FCSTD DOCUMENT  (FreeCAD 1.2R20251230 (Git shallow))
Label: smart_glasses_0
License: Creative Commons Attribution 4.0
LicenseURL: https://creativecommons.org/licenses/by/4.0/
objects: Sketcher::SketchObject×2, App::Point×1, PartDesign::Body×1
note: 5 computed .brp shape members not serialized (recipe doc carries the construction recipe); baked Part::Feature solids carry a one-line shape summary decoded from their .brp

FEATURE [App::Point] Origin001  label="原点"
  Role = Origin
FEATURE [Sketcher::SketchObject] Sketch
  ArcFitTolerance = 1e-06
  AttachmentSupport = -> [Origin]
  ExternalTypes = [0]
  FullyConstrained = false
  MakeInternals = false
  MapMode = 5
  sketch-geometry (83):
    g0: LineSegment StartX=-44.6431 StartY=-12.8691 StartZ=0 EndX=-49.4299 EndY=18.6606 EndZ=0
    g1: LineSegment StartX=-39.4718 StartY=40.2018 StartZ=0 EndX=-48.5995 EndY=23.3988 EndZ=0
    g2: LineSegment StartX=-37.4949 StartY=42.2431 StartZ=0 EndX=-35.6096 EndY=43.347 EndZ=0
    g3: LineSegment StartX=-34.9116 StartY=42.6805 StartZ=0 EndX=-45.8946 EndY=21.7585 EndZ=0
    g4: LineSegment StartX=-46.1795 StartY=20.2606 StartZ=0 EndX=-42.6348 EndY=-12.6091 EndZ=0
    g5: LineSegment StartX=-43.5009 StartY=-13.7035 StartZ=0 EndX=-43.5351 EndY=-13.7077 EndZ=0
    g6: ArcOfCircle CenterX=-41.9638 CenterY=19.7941 CenterZ=0 NormalX=0 NormalY=0 NormalZ=1 AngleXU=0 Radius=7.5516 StartAngle=2.64397 EndAngle=3.29226
    g7: GeomPoint [constr] X=-49.8107 Y=21.1692 Z=0
    g8: ArcOfCircle CenterX=-34.8202 CenterY=37.6749 CenterZ=0 NormalX=0 NormalY=0 NormalZ=1 AngleXU=0 Radius=5.29359 StartAngle=2.10048 EndAngle=2.64397
    g9: GeomPoint [constr] X=-38.7677 Y=41.4979 Z=0
    g10: ArcOfCircle CenterX=-35.356 CenterY=42.9138 CenterZ=0 NormalX=0 NormalY=0 NormalZ=1 AngleXU=0 Radius=0.501906 StartAngle=5.79978 EndAngle=8.38366
    g11: GeomPoint [constr] X=-34.0968 Y=44.2327 Z=0
    g12: ArcOfCircle CenterX=-43.576 CenterY=20.5414 CenterZ=0 NormalX=0 NormalY=0 NormalZ=1 AngleXU=0 Radius=2.61862 StartAngle=2.65819 EndAngle=3.24902
    g13: GeomPoint [constr] X=-46.265 Y=21.0529 Z=0
    g14: ArcOfCircle CenterX=-43.6244 CenterY=-12.7158 CenterZ=0 NormalX=0 NormalY=0 NormalZ=1 AngleXU=0 Radius=0.995334 StartAngle=4.83674 EndAngle=6.39061
    g15: GeomPoint [constr] X=-42.5298 Y=-13.5821 Z=0
    g16: ArcOfCircle CenterX=-43.6586 CenterY=-12.7196 CenterZ=0 NormalX=0 NormalY=0 NormalZ=1 AngleXU=0 Radius=0.995804 StartAngle=3.29226 EndAngle=4.83674
    g17: ArcOfCircle CenterX=35.3756 CenterY=33.9263 CenterZ=0 NormalX=0 NormalY=0 NormalZ=1 AngleXU=0 Radius=14.9602 StartAngle=0.189378 EndAngle=3.00877
    g18: ArcOfCircle CenterX=26.7496 CenterY=16.2061 CenterZ=0 NormalX=0 NormalY=0 NormalZ=1 AngleXU=0 Radius=7.90499 StartAngle=3.03877 EndAngle=5.2827
    g19: LineSegment StartX=-113.726 StartY=52.4777 StartZ=0 EndX=-93.6115 EndY=39.4134 EndZ=0
    g20: LineSegment StartX=-93.6115 StartY=39.4134 StartZ=0 EndX=-113.312 EndY=28.5265 EndZ=0
    g21: LineSegment StartX=-108.049 StartY=31.0762 StartZ=0 EndX=-78.0588 EndY=26.8676 EndZ=0
    g22: ArcOfEllipse CenterX=-126.741 CenterY=52.1553 CenterZ=0 NormalX=0 NormalY=0 NormalZ=1 MajorRadius=2.45999 MinorRadius=2.01302 AngleXU=-0.349856 StartAngle=5.95659 EndAngle=6.68646
    g23: LineSegment [constr] StartX=-124.43 StartY=51.3121 StartZ=0 EndX=-129.052 EndY=52.9985 EndZ=0
    g24: LineSegment [constr] StartX=-126.051 StartY=54.0464 StartZ=0 EndX=-127.431 EndY=50.2642 EndZ=0
    g25: GeomPoint [constr] X=-125.413 Y=51.6706 Z=0
    g26: GeomPoint [constr] X=-128.069 Y=52.64 Z=0
    g27: ArcOfEllipse CenterX=-115.561 CenterY=46.8151 CenterZ=0 NormalX=0 NormalY=0 NormalZ=1 MajorRadius=2.45932 MinorRadius=1.51775 AngleXU=-2.21018 StartAngle=2.49555 EndAngle=7.74185
    g28: LineSegment [constr] StartX=-117.028 StartY=44.8416 StartZ=0 EndX=-114.093 EndY=48.7886 EndZ=0
    g29: LineSegment [constr] StartX=-114.343 StartY=45.9094 StartZ=0 EndX=-116.779 EndY=47.7207 EndZ=0
    g30: GeomPoint [constr] X=-116.716 Y=45.2622 Z=0
    g31: GeomPoint [constr] X=-114.406 Y=48.368 Z=0
    g32: ArcOfCircle CenterX=-99.3737 CenterY=57.4862 CenterZ=0 NormalX=0 NormalY=0 NormalZ=1 AngleXU=0 Radius=3.25236 StartAngle=3.75206 EndAngle=5.09277
    g33: ArcOfParabola CenterX=-131.419 CenterY=69.631 CenterZ=0 NormalX=0 NormalY=0 NormalZ=1 Focal=4.59446 AngleXU=2.52724 StartAngle=-2.27497 EndAngle=-0.0447105
    g34: GeomPoint [constr] X=-135.174 Y=72.2794 Z=0
    g35: LineSegment [constr] StartX=-131.419 StartY=69.631 StartZ=0 EndX=-135.174 EndY=72.2794 EndZ=0
    g36: ArcOfParabola CenterX=-128.34 CenterY=69.7487 CenterZ=0 NormalX=0 NormalY=0 NormalZ=1 Focal=4.97602 AngleXU=2.86921 StartAngle=1.54307 EndAngle=1.92024
    g37: GeomPoint [constr] X=-133.133 Y=71.0874 Z=0
    g38: LineSegment [constr] StartX=-128.34 StartY=69.7487 StartZ=0 EndX=-133.133 EndY=71.0874 EndZ=0
    g39: Ellipse CenterX=-117.407 CenterY=70.4858 CenterZ=0 NormalX=0 NormalY=0 NormalZ=1 MajorRadius=4.9111 MinorRadius=1.89223 AngleXU=3.12808
    g40: LineSegment [constr] StartX=-122.318 StartY=70.5521 StartZ=0 EndX=-112.497 EndY=70.4194 EndZ=0
    g41: LineSegment [constr] StartX=-117.433 StartY=68.5937 StartZ=0 EndX=-117.382 EndY=72.3778 EndZ=0
    g42: GeomPoint [constr] X=-121.939 Y=70.547 Z=0
    g43: GeomPoint [constr] X=-112.876 Y=70.4245 Z=0
    g44: Ellipse CenterX=-118.404 CenterY=64.6562 CenterZ=0 NormalX=0 NormalY=0 NormalZ=1 MajorRadius=4.82559 MinorRadius=3.73689 AngleXU=2.91718
    g45: LineSegment [constr] StartX=-123.109 StartY=65.7301 StartZ=0 EndX=-113.7 EndY=63.5823 EndZ=0
    g46: LineSegment [constr] StartX=-119.236 StartY=61.013 StartZ=0 EndX=-117.573 EndY=68.2994 EndZ=0
    g47: GeomPoint [constr] X=-121.381 Y=65.3356 Z=0
    g48: GeomPoint [constr] X=-115.428 Y=63.9767 Z=0
    g49: LineSegment StartX=-140.751 StartY=67.5074 StartZ=0 EndX=-140.751 EndY=62.2907 EndZ=0
    g50: LineSegment StartX=-140.202 StartY=61.7414 StartZ=0 EndX=-138.693 EndY=61.7414 EndZ=0
    g51: LineSegment StartX=-138.143 StartY=62.2907 StartZ=0 EndX=-138.143 EndY=67.5074 EndZ=0
    g52: LineSegment StartX=-138.693 StartY=68.0568 StartZ=0 EndX=-140.202 EndY=68.0568 EndZ=0
    g53: ArcOfCircle CenterX=-140.202 CenterY=67.5074 CenterZ=0 NormalX=0 NormalY=0 NormalZ=1 AngleXU=0 Radius=0.549355 StartAngle=1.5708 EndAngle=3.14159
    g54: ArcOfCircle CenterX=-140.202 CenterY=62.2907 CenterZ=0 NormalX=0 NormalY=0 NormalZ=1 AngleXU=0 Radius=0.549355 StartAngle=3.14159 EndAngle=4.71239
    g55: ArcOfCircle CenterX=-138.693 CenterY=62.2907 CenterZ=0 NormalX=0 NormalY=0 NormalZ=1 AngleXU=0 Radius=0.549355 StartAngle=4.71239 EndAngle=6.28319
    g56: ArcOfCircle CenterX=-138.693 CenterY=67.5074 CenterZ=0 NormalX=0 NormalY=0 NormalZ=1 AngleXU=0 Radius=0.549355 StartAngle=0 EndAngle=1.5708
    g57: GeomPoint [constr] X=-140.751 Y=68.0568 Z=0
    g58: GeomPoint [constr] X=-138.143 Y=61.7414 Z=0
    g59: ArcOfCircle CenterX=-131.649 CenterY=63.6079 CenterZ=0 NormalX=0 NormalY=0 NormalZ=1 AngleXU=0 Radius=3.47763 StartAngle=2.83572 EndAngle=4.28444
    g60: ArcOfCircle CenterX=-132.978 CenterY=60.6931 CenterZ=0 NormalX=0 NormalY=0 NormalZ=1 AngleXU=0 Radius=0.273918 StartAngle=4.28444 EndAngle=7.42603
    g61: ArcOfCircle CenterX=-134.704 CenterY=64.5726 CenterZ=0 NormalX=0 NormalY=0 NormalZ=1 AngleXU=0 Radius=0.273918 StartAngle=5.97732 EndAngle=9.11891
    g62: ArcOfCircle CenterX=-131.649 CenterY=63.6079 CenterZ=0 NormalX=0 NormalY=0 NormalZ=1 AngleXU=0 Radius=2.92979 StartAngle=2.83572 EndAngle=4.28444
    g63-g71: Circle [constr] x9 (B-spline internal-alignment scaffolding for g72; pole/knot coordinates omitted)
    g72: BSplineCurve PolesCount=9 KnotsCount=10 Degree=3 IsPeriodic=1
    g73-g82: GeomPoint [constr] x10 (B-spline internal-alignment scaffolding for g72; pole/knot coordinates omitted)
  constraints (59):
    c: PointOnObject(g7,g1)
    c: PointOnObject(g7,g0)
    c: Tangent(g1,g6) = -1.5708
    c: Tangent(g0,g6) = 1.5708
    c: PointOnObject(g9,g1)
    c: Tangent(g1,g8) = -1.5708
    c: PointOnObject(g11,g2)
    c: PointOnObject(g11,g3)
    c: Tangent(g2,g10) = 1.5708
    c: Tangent(g3,g10) = 1.5708
    c: PointOnObject(g13,g3)
    c: PointOnObject(g13,g4)
    c: Tangent(g3,g12) = -1.5708
    c: Tangent(g4,g12) = -1.5708
    c: PointOnObject(g15,g4)
    c: PointOnObject(g15,g5)
    c: Tangent(g4,g14) = 1.5708
    c: Tangent(g5,g14) = 1.5708
    c: Tangent(g0,g16) = 1.5708
    c: Tangent(g5,g16) = 1.5708
    c: Coincident(g20,g19)
    c: InternalAlignment(g23-g26 -> g22) x4
    c: InternalAlignment(g28-g31 -> g27) x4
    c: InternalAlignment(g34,g33)
    c: InternalAlignment(g35,g33)
    c: InternalAlignment(g37,g36)
    c: InternalAlignment(g38,g36)
    c: PointOnObject(g36,g35)
    c: InternalAlignment(g40-g43 -> g39) x4
    c: InternalAlignment(g45-g48 -> g44) x4
    c: Tangent(g49,g53) = -1.5708
    c: Tangent(g49,g54) = -1.5708
    c: Tangent(g50,g54) = -1.5708
    c: Tangent(g50,g55) = -1.5708
    c: Tangent(g51,g55) = -1.5708
    c: Tangent(g51,g56) = -1.5708
    c: Tangent(g52,g56) = -1.5708
    c: Tangent(g52,g53) = -1.5708
    c: Vertical(g49)
    c: Vertical(g51)
    c: Horizontal(g50)
    c: Horizontal(g52)
    c: Equal(g53,g54)
    c: Equal(g54,g55)
    c: Equal(g55,g56)
    c: PointOnObject(g57,g49)
    c: PointOnObject(g57,g52)
    c: PointOnObject(g58,g50)
    c: PointOnObject(g58,g51)
    c: Coincident(g59,g62)
    c: Tangent(g62,g61) = 1.5708
    c: Tangent(g62,g60) = 1.5708
    c: Tangent(g59,g61) = -1.5708
    c: Tangent(g59,g60) = -1.5708
    c: Weight(g63) = 1
    c: Equal(g63, g64-g71) x8
    c: InternalAlignment(g63-g71 -> g72) x9
    c: InternalAlignment(g73-g82 -> g72) x10
    c: PointOnObject(g65,g63)
FEATURE [Sketcher::SketchObject] Sketch001
  ArcFitTolerance = 1e-06
  AttachmentSupport = -> [Origin]
  ExternalTypes = [0]
  FullyConstrained = false
  MakeInternals = false
  MapMode = 5
  sketch-geometry (132):
    g0: LineSegment StartX=-179.096 StartY=100.414 StartZ=0 EndX=-133.628 EndY=107.258 EndZ=0
    g1: LineSegment StartX=-133.628 StartY=107.258 StartZ=0 EndX=-131.954 EndY=85.1217 EndZ=0
    g2: LineSegment StartX=-131.954 StartY=85.1217 StartZ=0 EndX=-85.4499 EndY=81.0294 EndZ=0
    g3: LineSegment StartX=-85.4499 StartY=81.0294 StartZ=0 EndX=-101.633 EndY=62.2129 EndZ=0
    g4: LineSegment StartX=-101.633 StartY=62.2129 StartZ=0 EndX=-169.157 EndY=62.2129 EndZ=0
    g5: LineSegment StartX=-169.157 StartY=62.2129 StartZ=0 EndX=-179.096 EndY=100.414 EndZ=0
    g6: LineSegment StartX=-171.369 StartY=43.8261 StartZ=0 EndX=-101.654 EndY=43.8261 EndZ=0
    g7: ArcOfCircle CenterX=80.0712 CenterY=191.162 CenterZ=0 NormalX=0 NormalY=0 NormalZ=1 AngleXU=0 Radius=10 StartAngle=5.44193 EndAngle=7.53633
    g8: ArcOfCircle CenterX=137.521 CenterY=114.594 CenterZ=0 NormalX=0 NormalY=0 NormalZ=1 AngleXU=0 Radius=8.45744 StartAngle=3.76206 EndAngle=7.56382
    g9: ArcOfEllipse CenterX=195.187 CenterY=133.858 CenterZ=0 NormalX=0 NormalY=0 NormalZ=1 MajorRadius=31.4877 MinorRadius=12.413 AngleXU=-1.90676 StartAngle=1.03899 EndAngle=4.30453
    g10: LineSegment [constr] StartX=184.806 StartY=104.131 StartZ=0 EndX=205.568 EndY=163.586 EndZ=0
    g11: LineSegment [constr] StartX=206.906 StartY=129.766 StartZ=0 EndX=183.468 EndY=137.951 EndZ=0
    g12: GeomPoint [constr] X=185.647 Y=106.539 Z=0
    g13: GeomPoint [constr] X=204.728 Y=161.178 Z=0
    g14: Circle CenterX=54.931 CenterY=95.725 CenterZ=0 NormalX=0 NormalY=0 NormalZ=1 AngleXU=0 Radius=12.9332
    g15: Circle CenterX=95.9598 CenterY=131.115 CenterZ=0 NormalX=0 NormalY=0 NormalZ=1 AngleXU=0 Radius=21.3432
    g16: Ellipse CenterX=165.425 CenterY=181.665 CenterZ=0 NormalX=0 NormalY=0 NormalZ=1 MajorRadius=13.6492 MinorRadius=11.0941 AngleXU=-2.53499
    g17: LineSegment [constr] StartX=154.211 StartY=173.883 StartZ=0 EndX=176.639 EndY=189.446 EndZ=0
    g18: LineSegment [constr] StartX=171.749 StartY=172.55 StartZ=0 EndX=159.1 EndY=190.779 EndZ=0
    g19: GeomPoint [constr] X=158.892 Y=177.132 Z=0
    g20: GeomPoint [constr] X=171.957 Y=186.197 Z=0
    g21: Ellipse CenterX=127.198 CenterY=157.762 CenterZ=0 NormalX=0 NormalY=0 NormalZ=1 MajorRadius=15.291 MinorRadius=8.35315 AngleXU=0.65909
    g22: LineSegment [constr] StartX=139.287 StartY=167.126 StartZ=0 EndX=115.11 EndY=148.397 EndZ=0
    g23: LineSegment [constr] StartX=122.083 StartY=164.365 StartZ=0 EndX=132.314 EndY=151.158 EndZ=0
    g24: GeomPoint [constr] X=137.324 Y=165.605 Z=0
    g25: GeomPoint [constr] X=117.073 Y=149.918 Z=0
    g26: LineSegment StartX=47.3976 StartY=-33.3055 StartZ=0 EndX=47.3976 EndY=-42.2341 EndZ=0
    g27: LineSegment StartX=51.8487 StartY=-46.6851 StartZ=0 EndX=57.1613 EndY=-46.6851 EndZ=0
    g28: LineSegment StartX=61.6123 StartY=-42.2341 StartZ=0 EndX=61.6123 EndY=-33.3055 EndZ=0
    g29: LineSegment StartX=57.1613 StartY=-28.8544 StartZ=0 EndX=51.8487 EndY=-28.8544 EndZ=0
    g30: ArcOfCircle CenterX=51.8487 CenterY=-33.3055 CenterZ=0 NormalX=0 NormalY=0 NormalZ=1 AngleXU=0 Radius=4.45108 StartAngle=1.5708 EndAngle=3.14159
    g31: ArcOfCircle CenterX=51.8487 CenterY=-42.2341 CenterZ=0 NormalX=0 NormalY=0 NormalZ=1 AngleXU=0 Radius=4.45108 StartAngle=3.14159 EndAngle=4.71239
    g32: ArcOfCircle CenterX=57.1613 CenterY=-42.2341 CenterZ=0 NormalX=0 NormalY=0 NormalZ=1 AngleXU=0 Radius=4.45108 StartAngle=4.71239 EndAngle=6.28319
    g33: ArcOfCircle CenterX=57.1613 CenterY=-33.3055 CenterZ=0 NormalX=0 NormalY=0 NormalZ=1 AngleXU=0 Radius=4.45108 StartAngle=0 EndAngle=1.5708
    g34: GeomPoint [constr] X=47.3976 Y=-28.8544 Z=0
    g35: GeomPoint [constr] X=61.6123 Y=-46.6851 Z=0
    g36: LineSegment StartX=120.217 StartY=-40.0765 StartZ=0 EndX=120.217 EndY=-61.8974 EndZ=0
    g37: LineSegment StartX=120.217 StartY=-61.8974 StartZ=0 EndX=151.39 EndY=-61.8974 EndZ=0
    g38: LineSegment StartX=151.39 StartY=-61.8974 StartZ=0 EndX=151.39 EndY=-40.0765 EndZ=0
    g39: LineSegment StartX=151.39 StartY=-40.0765 StartZ=0 EndX=120.217 EndY=-40.0765 EndZ=0
    g40: LineSegment StartX=56.126 StartY=-66.885 StartZ=0 EndX=56.126 EndY=-84.0923 EndZ=0
    g41: LineSegment StartX=56.126 StartY=-84.0923 StartZ=0 EndX=93.7825 EndY=-84.0923 EndZ=0
    g42: LineSegment StartX=93.7825 StartY=-84.0923 StartZ=0 EndX=93.7825 EndY=-66.885 EndZ=0
    g43: LineSegment StartX=93.7825 StartY=-66.885 StartZ=0 EndX=56.126 EndY=-66.885 EndZ=0
    g44: GeomPoint [constr] X=74.9542 Y=-75.4887 Z=0
    g45: LineSegment StartX=-629.082 StartY=-206.086 StartZ=0 EndX=-663.995 EndY=-61.1739 EndZ=0
    g46: LineSegment StartX=-663.995 StartY=-61.1739 StartZ=0 EndX=-772.036 EndY=-163.866 EndZ=0
    g47: LineSegment StartX=-772.036 StartY=-163.866 StartZ=0 EndX=-629.082 EndY=-206.086 EndZ=0
    g48: Circle [constr] CenterX=-688.371 CenterY=-143.709 CenterZ=0 NormalX=0 NormalY=0 NormalZ=1 AngleXU=0 Radius=86.0589
    g49: LineSegment StartX=-350.546 StartY=-239.436 StartZ=0 EndX=-378.338 EndY=-68.3619 EndZ=0
    g50: LineSegment StartX=-378.338 StartY=-68.3619 StartZ=0 EndX=-549.412 EndY=-96.1537 EndZ=0
    g51: LineSegment StartX=-549.412 StartY=-96.1537 StartZ=0 EndX=-521.62 EndY=-267.228 EndZ=0
    g52: LineSegment StartX=-521.62 StartY=-267.228 StartZ=0 EndX=-350.546 EndY=-239.436 EndZ=0
    g53: Circle [constr] CenterX=-449.979 CenterY=-167.795 CenterZ=0 NormalX=0 NormalY=0 NormalZ=1 AngleXU=0 Radius=122.554
    g54: LineSegment StartX=-661.197 StartY=-493.268 StartZ=0 EndX=-642.21 EndY=-409.175 EndZ=0
    g55: LineSegment StartX=-642.21 StartY=-409.175 StartZ=0 EndX=-696.119 EndY=-341.9 EndZ=0
    g56: LineSegment StartX=-696.119 StartY=-341.9 StartZ=0 EndX=-782.328 EndY=-342.101 EndZ=0
    g57: LineSegment StartX=-782.328 StartY=-342.101 StartZ=0 EndX=-835.921 EndY=-409.628 EndZ=0
    g58: LineSegment StartX=-835.921 StartY=-409.628 StartZ=0 EndX=-816.541 EndY=-493.632 EndZ=0
    g59: LineSegment StartX=-816.541 StartY=-493.632 StartZ=0 EndX=-738.781 EndY=-530.855 EndZ=0
    g60: LineSegment StartX=-738.781 StartY=-530.855 StartZ=0 EndX=-661.197 EndY=-493.268 EndZ=0
    g61: Circle [constr] CenterX=-739.014 CenterY=-431.508 CenterZ=0 NormalX=0 NormalY=0 NormalZ=1 AngleXU=0 Radius=99.3466
    g62: LineSegment StartX=-311.02 StartY=-522.913 StartZ=0 EndX=-280.576 EndY=-458.333 EndZ=0
    g63: LineSegment StartX=-280.576 StartY=-458.333 StartZ=0 EndX=-298.766 EndY=-389.293 EndZ=0
    g64: LineSegment StartX=-298.766 StartY=-389.293 StartZ=0 EndX=-357.078 EndY=-348.098 EndZ=0
    g65: LineSegment StartX=-357.078 StartY=-348.098 StartZ=0 EndX=-428.228 EndY=-354.023 EndZ=0
    g66: LineSegment StartX=-428.228 StartY=-354.023 StartZ=0 EndX=-478.923 EndY=-404.296 EndZ=0
    g67: LineSegment StartX=-478.923 StartY=-404.296 StartZ=0 EndX=-485.443 EndY=-475.393 EndZ=0
    g68: LineSegment StartX=-485.443 StartY=-475.393 StartZ=0 EndX=-444.737 EndY=-534.048 EndZ=0
    g69: LineSegment StartX=-444.737 StartY=-534.048 StartZ=0 EndX=-375.852 EndY=-552.815 EndZ=0
    g70: LineSegment StartX=-375.852 StartY=-552.815 StartZ=0 EndX=-311.02 EndY=-522.913 EndZ=0
    g71: Circle [constr] CenterX=-384.514 CenterY=-448.801 CenterZ=0 NormalX=0 NormalY=0 NormalZ=1 AngleXU=0 Radius=104.374
    g72: ArcOfCircle CenterX=-661.197 CenterY=-645.814 CenterZ=0 NormalX=0 NormalY=0 NormalZ=1 AngleXU=0 Radius=43.0061 StartAngle=1.50755 EndAngle=4.64914
    g73: ArcOfCircle CenterX=-475.918 CenterY=-657.549 CenterZ=0 NormalX=0 NormalY=0 NormalZ=1 AngleXU=0 Radius=43.0061 StartAngle=4.64914 EndAngle=7.79073
    g74: LineSegment StartX=-658.479 StartY=-602.894 StartZ=0 EndX=-473.2 EndY=-614.629 EndZ=0
    g75: LineSegment StartX=-663.915 StartY=-688.734 StartZ=0 EndX=-478.636 EndY=-700.469 EndZ=0
    g76: ArcOfCircle CenterX=-2011.29 CenterY=1760.95 CenterZ=0 NormalX=0 NormalY=0 NormalZ=1 AngleXU=0 Radius=100 StartAngle=1.41132 EndAngle=4.55291
    g77: ArcOfCircle CenterX=-1511.29 CenterY=1680.53 CenterZ=0 NormalX=0 NormalY=0 NormalZ=1 AngleXU=0 Radius=100 StartAngle=4.55291 EndAngle=7.6945
    g78: LineSegment StartX=-1995.41 StartY=1859.68 StartZ=0 EndX=-1495.41 EndY=1779.26 EndZ=0
    g79: LineSegment StartX=-2027.17 StartY=1662.22 StartZ=0 EndX=-1527.17 EndY=1581.8 EndZ=0
    g80: ArcOfCircle CenterX=-2249.55 CenterY=1202.8 CenterZ=0 NormalX=0 NormalY=0 NormalZ=1 AngleXU=0 Radius=258.116 StartAngle=4.39919 EndAngle=5.96613
    g81: ArcOfCircle CenterX=-2118.32 CenterY=1159.74 CenterZ=0 NormalX=0 NormalY=0 NormalZ=1 AngleXU=0 Radius=120 StartAngle=5.96613 EndAngle=9.10772
    g82: ArcOfCircle CenterX=-2292.1 CenterY=1071.4 CenterZ=0 NormalX=0 NormalY=0 NormalZ=1 AngleXU=0 Radius=120 StartAngle=1.25759 EndAngle=4.39919
    g83: ArcOfCircle CenterX=-2249.55 CenterY=1202.8 CenterZ=0 NormalX=0 NormalY=0 NormalZ=1 AngleXU=0 Radius=18.1157 StartAngle=4.39919 EndAngle=5.96613
    g84: ArcOfCircle CenterX=-1296.14 CenterY=942.451 CenterZ=0 NormalX=0 NormalY=0 NormalZ=1 AngleXU=0 Radius=264.957 StartAngle=0.28493 EndAngle=2.55295
    g85: ArcOfCircle CenterX=-1118.64 CenterY=994.441 CenterZ=0 NormalX=0 NormalY=0 NormalZ=1 AngleXU=0 Radius=80 StartAngle=3.42652 EndAngle=6.56811
    g86: ArcOfCircle CenterX=-1449.97 CenterY=1045.15 CenterZ=0 NormalX=0 NormalY=0 NormalZ=1 AngleXU=0 Radius=80 StartAngle=2.55295 EndAngle=5.69454
    g87: ArcOfCircle CenterX=-1296.14 CenterY=942.451 CenterZ=0 NormalX=0 NormalY=0 NormalZ=1 AngleXU=0 Radius=104.957 StartAngle=0.28493 EndAngle=2.55295
    g88: LineSegment StartX=-1134.08 StartY=2205.49 StartZ=0 EndX=-500.48 EndY=2205.49 EndZ=0
    g89: LineSegment StartX=-912.628 StartY=2369.53 StartZ=0 EndX=-912.628 EndY=2010.69 EndZ=0
    g90: LineSegment StartX=-1562.63 StartY=1207.41 StartZ=0 EndX=-906.477 EndY=1207.41 EndZ=0
    g91: ArcOfCircle CenterX=413.213 CenterY=2914.61 CenterZ=0 NormalX=0 NormalY=0 NormalZ=1 AngleXU=0 Radius=286.747 StartAngle=6.02951 EndAngle=7.13515
    g92: ArcOfCircle CenterX=634.666 CenterY=2857.2 CenterZ=0 NormalX=0 NormalY=0 NormalZ=1 AngleXU=0 Radius=57.9718 StartAngle=2.88792 EndAngle=6.02951
    g93: ArcOfCircle CenterX=563.862 CenterY=3086.78 CenterZ=0 NormalX=0 NormalY=0 NormalZ=1 AngleXU=0 Radius=57.9718 StartAngle=0.851965 EndAngle=3.99356
    g94: ArcOfCircle CenterX=413.213 CenterY=2914.61 CenterZ=0 NormalX=0 NormalY=0 NormalZ=1 AngleXU=0 Radius=170.803 StartAngle=6.02951 EndAngle=7.13515
    g95: ArcOfCircle CenterX=804.905 CenterY=2914.61 CenterZ=0 NormalX=0 NormalY=0 NormalZ=1 AngleXU=0 Radius=286.747 StartAngle=6.02951 EndAngle=7.13515
    g96: ArcOfCircle CenterX=1026.36 CenterY=2857.2 CenterZ=0 NormalX=0 NormalY=0 NormalZ=1 AngleXU=0 Radius=57.9718 StartAngle=2.88792 EndAngle=6.02951
    g97: ArcOfCircle CenterX=955.554 CenterY=3086.78 CenterZ=0 NormalX=0 NormalY=0 NormalZ=1 AngleXU=0 Radius=57.9718 StartAngle=0.851965 EndAngle=3.99356
    g98: ArcOfCircle CenterX=804.905 CenterY=2914.61 CenterZ=0 NormalX=0 NormalY=0 NormalZ=1 AngleXU=0 Radius=170.803 StartAngle=6.02951 EndAngle=7.13515
    g99: ArcOfCircle CenterX=1196.6 CenterY=2914.61 CenterZ=0 NormalX=0 NormalY=0 NormalZ=1 AngleXU=0 Radius=286.746 StartAngle=6.02951 EndAngle=7.13515
    g100: ArcOfCircle CenterX=1418.05 CenterY=2857.2 CenterZ=0 NormalX=0 NormalY=0 NormalZ=1 AngleXU=0 Radius=57.9717 StartAngle=2.88792 EndAngle=6.02951
    g101: ArcOfCircle CenterX=1347.25 CenterY=3086.78 CenterZ=0 NormalX=0 NormalY=0 NormalZ=1 AngleXU=0 Radius=57.9717 StartAngle=0.851965 EndAngle=3.99356
    g102: ArcOfCircle CenterX=1196.6 CenterY=2914.61 CenterZ=0 NormalX=0 NormalY=0 NormalZ=1 AngleXU=0 Radius=170.803 StartAngle=6.02951 EndAngle=7.13515
    g103: ArcOfCircle CenterX=1588.29 CenterY=2914.61 CenterZ=0 NormalX=0 NormalY=0 NormalZ=1 AngleXU=0 Radius=286.746 StartAngle=6.02951 EndAngle=7.13515
    g104: ArcOfCircle CenterX=1809.74 CenterY=2857.2 CenterZ=0 NormalX=0 NormalY=0 NormalZ=1 AngleXU=0 Radius=57.9717 StartAngle=2.88792 EndAngle=6.02951
    g105: ArcOfCircle CenterX=1738.94 CenterY=3086.78 CenterZ=0 NormalX=0 NormalY=0 NormalZ=1 AngleXU=0 Radius=57.9717 StartAngle=0.851965 EndAngle=3.99356
    g106: ArcOfCircle CenterX=1588.29 CenterY=2914.61 CenterZ=0 NormalX=0 NormalY=0 NormalZ=1 AngleXU=0 Radius=170.803 StartAngle=6.02951 EndAngle=7.13515
    g107: ArcOfCircle CenterX=724.887 CenterY=1883.21 CenterZ=0 NormalX=0 NormalY=0 NormalZ=1 AngleXU=0 Radius=286.747 StartAngle=6.02951 EndAngle=7.13515
    g108: ArcOfCircle CenterX=946.341 CenterY=1825.8 CenterZ=0 NormalX=0 NormalY=0 NormalZ=1 AngleXU=0 Radius=57.9718 StartAngle=2.88792 EndAngle=6.02951
    g109: ArcOfCircle CenterX=875.537 CenterY=2055.39 CenterZ=0 NormalX=0 NormalY=0 NormalZ=1 AngleXU=0 Radius=57.9718 StartAngle=0.851965 EndAngle=3.99356
    g110: ArcOfCircle CenterX=724.887 CenterY=1883.21 CenterZ=0 NormalX=0 NormalY=0 NormalZ=1 AngleXU=0 Radius=170.803 StartAngle=6.02951 EndAngle=7.13515
    g111: ArcOfCircle CenterX=1116.58 CenterY=1883.21 CenterZ=0 NormalX=0 NormalY=0 NormalZ=1 AngleXU=0 Radius=286.746 StartAngle=6.02951 EndAngle=7.13515
    g112: ArcOfCircle CenterX=1338.03 CenterY=1825.8 CenterZ=0 NormalX=0 NormalY=0 NormalZ=1 AngleXU=0 Radius=57.9717 StartAngle=2.88792 EndAngle=6.02951
    g113: ArcOfCircle CenterX=1267.23 CenterY=2055.38 CenterZ=0 NormalX=0 NormalY=0 NormalZ=1 AngleXU=0 Radius=57.9717 StartAngle=0.851965 EndAngle=3.99356
    g114: ArcOfCircle CenterX=1116.58 CenterY=1883.21 CenterZ=0 NormalX=0 NormalY=0 NormalZ=1 AngleXU=0 Radius=170.803 StartAngle=6.02951 EndAngle=7.13515
    g115: ArcOfCircle CenterX=1508.27 CenterY=1883.21 CenterZ=0 NormalX=0 NormalY=0 NormalZ=1 AngleXU=0 Radius=286.747 StartAngle=6.02951 EndAngle=7.13515
    g116: ArcOfCircle CenterX=1729.73 CenterY=1825.8 CenterZ=0 NormalX=0 NormalY=0 NormalZ=1 AngleXU=0 Radius=57.9718 StartAngle=2.88792 EndAngle=6.02951
    g117: ArcOfCircle CenterX=1658.92 CenterY=2055.39 CenterZ=0 NormalX=0 NormalY=0 NormalZ=1 AngleXU=0 Radius=57.9718 StartAngle=0.851965 EndAngle=3.99356
    g118: ArcOfCircle CenterX=1508.27 CenterY=1883.21 CenterZ=0 NormalX=0 NormalY=0 NormalZ=1 AngleXU=0 Radius=170.803 StartAngle=6.02951 EndAngle=7.13515
    g119: ArcOfCircle CenterX=1899.96 CenterY=1883.21 CenterZ=0 NormalX=0 NormalY=0 NormalZ=1 AngleXU=0 Radius=286.746 StartAngle=6.02951 EndAngle=7.13515
    g120: ArcOfCircle CenterX=2121.42 CenterY=1825.8 CenterZ=0 NormalX=0 NormalY=0 NormalZ=1 AngleXU=0 Radius=57.9717 StartAngle=2.88792 EndAngle=6.02951
    g121: ArcOfCircle CenterX=2050.61 CenterY=2055.39 CenterZ=0 NormalX=0 NormalY=0 NormalZ=1 AngleXU=0 Radius=57.9717 StartAngle=0.851965 EndAngle=3.99356
    g122: ArcOfCircle CenterX=1899.96 CenterY=1883.21 CenterZ=0 NormalX=0 NormalY=0 NormalZ=1 AngleXU=0 Radius=170.803 StartAngle=6.02951 EndAngle=7.13515
    g123: ArcOfCircle CenterX=2291.66 CenterY=1883.21 CenterZ=0 NormalX=0 NormalY=0 NormalZ=1 AngleXU=0 Radius=286.747 StartAngle=6.02951 EndAngle=7.13515
    g124: ArcOfCircle CenterX=2513.11 CenterY=1825.8 CenterZ=0 NormalX=0 NormalY=0 NormalZ=1 AngleXU=0 Radius=57.9718 StartAngle=2.88792 EndAngle=6.02951
    g125: ArcOfCircle CenterX=2442.31 CenterY=2055.39 CenterZ=0 NormalX=0 NormalY=0 NormalZ=1 AngleXU=0 Radius=57.9718 StartAngle=0.851965 EndAngle=3.99356
    g126: ArcOfCircle CenterX=2291.66 CenterY=1883.21 CenterZ=0 NormalX=0 NormalY=0 NormalZ=1 AngleXU=0 Radius=170.803 StartAngle=6.02951 EndAngle=7.13515
    g127: ArcOfCircle CenterX=1658.67 CenterY=3649.49 CenterZ=0 NormalX=0 NormalY=0 NormalZ=1 AngleXU=0 Radius=512.452 StartAngle=5.17351 EndAngle=6.27915
    g128: ArcOfCircle CenterX=1840.59 CenterY=3283.34 CenterZ=0 NormalX=0 NormalY=0 NormalZ=1 AngleXU=0 Radius=103.603 StartAngle=2.03192 EndAngle=5.17351
    g129: ArcOfCircle CenterX=2067.52 CenterY=3647.84 CenterZ=0 NormalX=0 NormalY=0 NormalZ=1 AngleXU=0 Radius=103.603 StartAngle=6.27915 EndAngle=9.42074
    g130: ArcOfCircle CenterX=1658.67 CenterY=3649.49 CenterZ=0 NormalX=0 NormalY=0 NormalZ=1 AngleXU=0 Radius=305.247 StartAngle=5.17351 EndAngle=6.27915
    g131: LineSegment StartX=2044.43 StartY=4106.5 StartZ=0 EndX=2932.16 EndY=3480.77 EndZ=0
  constraints (180):
    c: Coincident(g0,g1)
    c: Coincident(g1,g2)
    c: Coincident(g2,g3)
    c: Coincident(g3,g4)
    c: Coincident(g4,g5)
    c: Coincident(g5,g0)
    c: Horizontal(g6)
    c: Parallel(g4,g6)
    c: Radius(g7) = 10
    c: Angle(g7) = 2.0944
    c: InternalAlignment(g10-g13 -> g9) x4
    c: InternalAlignment(g17-g20 -> g16) x4
    c: InternalAlignment(g22-g25 -> g21) x4
    c: Tangent(g26,g30) = -1.5708
    c: Tangent(g26,g31) = -1.5708
    c: Tangent(g27,g31) = -1.5708
    c: Tangent(g27,g32) = -1.5708
    c: Tangent(g28,g32) = -1.5708
    c: Tangent(g28,g33) = -1.5708
    c: Tangent(g29,g33) = -1.5708
    c: Tangent(g29,g30) = -1.5708
    c: Vertical(g26)
    c: Vertical(g28)
    c: Horizontal(g27)
    c: Horizontal(g29)
    c: Equal(g30,g31)
    c: Equal(g31,g32)
    c: Equal(g32,g33)
    c: PointOnObject(g34,g26)
    c: PointOnObject(g34,g29)
    c: PointOnObject(g35,g27)
    c: PointOnObject(g35,g28)
    c: Coincident(g36,g37)
    c: Coincident(g37,g38)
    c: Coincident(g38,g39)
    c: Coincident(g39,g36)
    c: Vertical(g36)
    c: Vertical(g38)
    c: Horizontal(g37)
    c: Horizontal(g39)
    c: Coincident(g40,g41)
    c: Coincident(g41,g42)
    c: Coincident(g42,g43)
    c: Coincident(g43,g40)
    c: Vertical(g40)
    c: Vertical(g42)
    c: Horizontal(g41)
    c: Horizontal(g43)
    c: Symmetric(g42,g40,g44)
    c: Coincident(g45,g46)
    c: Coincident(g46,g47)
    c: Coincident(g47,g45)
    c: Equal(g45,g46)
    c: Equal(g45,g47)
    c: PointOnObject(g45,g48)
    c: PointOnObject(g46,g48)
    c: PointOnObject(g47,g48)
    c: Coincident(g49,g50)
    c: Coincident(g50,g51)
    c: Coincident(g51,g52)
    c: Coincident(g52,g49)
    c: Equal(g49,g50)
    c: Equal(g49,g51)
    c: Equal(g49,g52)
    c: PointOnObject(g49,g53)
    c: PointOnObject(g50,g53)
    c: PointOnObject(g51,g53)
    c: PointOnObject(g52,g53)
    c: Coincident(g54,g55)
    c: Coincident(g55,g56)
    c: Coincident(g56,g57)
    c: Coincident(g57,g58)
    c: Coincident(g58,g59)
    c: Coincident(g59,g60)
    c: Coincident(g60,g54)
    c: Equal(g54, g55-g60) x6
    c: PointOnObject(g54,g61)
    c: PointOnObject(g55,g61)
    c: PointOnObject(g56,g61)
    c: PointOnObject(g57,g61)
    c: PointOnObject(g58,g61)
    c: PointOnObject(g59,g61)
    c: PointOnObject(g60,g61)
    c: Coincident(g62,g63)
    c: Coincident(g63,g64)
    c: Coincident(g64,g65)
    c: Coincident(g65,g66)
    c: Coincident(g66,g67)
    c: Coincident(g67,g68)
    c: Coincident(g68,g69)
    c: Coincident(g69,g70)
    c: Coincident(g70,g62)
    c: Equal(g62, g63-g70) x8
    c: PointOnObject(g62,g71)
    c: PointOnObject(g63,g71)
    c: PointOnObject(g64,g71)
    c: PointOnObject(g65,g71)
    c: PointOnObject(g66,g71)
    c: PointOnObject(g67,g71)
    c: PointOnObject(g68,g71)
    c: PointOnObject(g69,g71)
    c: PointOnObject(g70,g71)
    c: Tangent(g72,g74) = 1.5708
    c: Tangent(g72,g75) = -1.5708
    c: Tangent(g73,g74) = 1.5708
    c: Tangent(g73,g75) = -1.5708
    c: Equal(g72,g73)
    c: Tangent(g76,g78) = 1.5708
    c: Tangent(g76,g79) = -1.5708
    c: Tangent(g77,g78) = 1.5708
    c: Tangent(g77,g79) = -1.5708
    c: Equal(g76,g77)
    c: DistanceX(g78,g78) = 500
    c: Radius(g77) = 100
    c: Coincident(g80,g83)
    c: Tangent(g83,g82) = 1.5708
    c: Tangent(g83,g81) = 1.5708
    c: Tangent(g80,g82) = -1.5708
    c: Tangent(g80,g81) = -1.5708
    c: Radius(g82) = 120
    c: Coincident(g84,g87)
    c: Tangent(g87,g86) = 1.5708
    c: Tangent(g87,g85) = 1.5708
    c: Tangent(g84,g86) = -1.5708
    c: Tangent(g84,g85) = -1.5708
    c: Radius(g85) = 80
    c: Vertical(g89)
    c: Horizontal(g88)
    c: Horizontal(g90)
    c: Tangent(g84,g90)
    c: Coincident(g91,g94)
    c: Tangent(g94,g93) = 1.5708
    c: Tangent(g94,g92) = 1.5708
    c: Tangent(g91,g93) = -1.5708
    c: Tangent(g91,g92) = -1.5708
    c: Coincident(g95,g98)
    c: Coincident(g99,g102)
    c: Coincident(g103,g106)
    c: Coincident(g107,g110)
    c: Coincident(g111,g114)
    c: Coincident(g115,g118)
    c: Coincident(g119,g122)
    c: Coincident(g123,g126)
    c: Tangent(g98,g97) = 1.5708
    c: Tangent(g102,g101) = 1.5708
    c: Tangent(g106,g105) = 1.5708
    c: Tangent(g110,g109) = 1.5708
    c: Tangent(g114,g113) = 1.5708
    c: Tangent(g118,g117) = 1.5708
    c: Tangent(g122,g121) = 1.5708
    c: Tangent(g126,g125) = 1.5708
    c: Tangent(g98,g96) = 1.5708
    c: Tangent(g102,g100) = 1.5708
    c: Tangent(g106,g104) = 1.5708
    c: Tangent(g110,g108) = 1.5708
    c: Tangent(g114,g112) = 1.5708
    c: Tangent(g118,g116) = 1.5708
    c: Tangent(g122,g120) = 1.5708
    c: Tangent(g126,g124) = 1.5708
    c: Tangent(g95,g97) = -1.5708
    c: Tangent(g99,g101) = -1.5708
    c: Tangent(g103,g105) = -1.5708
    c: Tangent(g107,g109) = -1.5708
    c: Tangent(g111,g113) = -1.5708
    c: Tangent(g115,g117) = -1.5708
    c: Tangent(g119,g121) = -1.5708
    c: Tangent(g123,g125) = -1.5708
    c: Tangent(g95,g96) = -1.5708
    c: Tangent(g99,g100) = -1.5708
    c: Tangent(g103,g104) = -1.5708
    c: Tangent(g107,g108) = -1.5708
    c: Tangent(g111,g112) = -1.5708
    c: Tangent(g115,g116) = -1.5708
    c: Tangent(g119,g120) = -1.5708
    c: Tangent(g123,g124) = -1.5708
    c: Coincident(g127,g130)
    c: Tangent(g130,g129) = 1.5708
    c: Tangent(g130,g128) = 1.5708
    c: Tangent(g127,g129) = -1.5708
    c: Tangent(g127,g128) = -1.5708
FEATURE [PartDesign::Body] Body
  AllowCompound = true
  Group = -> [Sketch,Sketch001]
  Origin = -> Origin
